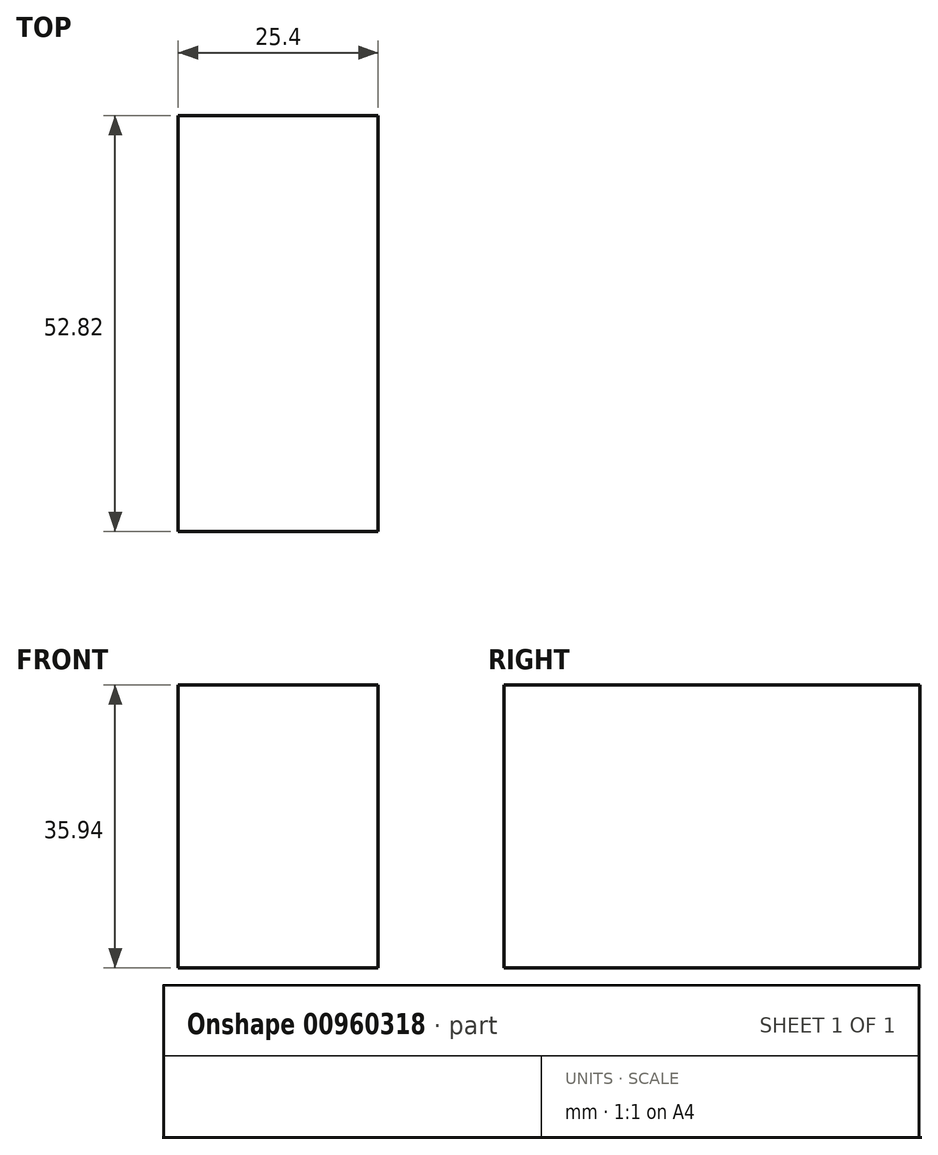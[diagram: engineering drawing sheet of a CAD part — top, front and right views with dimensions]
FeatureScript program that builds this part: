
annotation { "Feature Type Name" : "Feature", "Feature Type Description" : "" }
export const myFeature = defineFeature(function(context is Context, id is Id, definition is map)
    precondition{}
    {
        {
            var Q0;
            Q0=qCreatedBy(makeId("Right.planeOp"),FACE);
            var sketch = newSketch(context, id + "F0", { "sketchPlane" : qUnion([Q0])});
            skLineSegment(sketch, "E0.bottom", {"start": v(26.41, 17.97) * mm, "end": v(-26.41, 17.97) * mm});
            skLineSegment(sketch, "E0.top", {"start": v(26.41, -17.97) * mm, "end": v(-26.41, -17.97) * mm});
            skLineSegment(sketch, "E0.left", {"start": v(26.41, 17.97) * mm, "end": v(26.41, -17.97) * mm});
            skLineSegment(sketch, "E0.right", {"start": v(-26.41, 17.97) * mm, "end": v(-26.41, -17.97) * mm});
            skPoint(sketch, "E0.middle", {"position": v(0, 0) * mm});
            skSolve(sketch);
        }
        {
            var Q0;
            Q0=makeQuery(id+"F0.imprint","IMPRINT",FACE,{"disambiguationData":[TD([[makeQuery(id+"F0.imprint","IMPRINT",EDGE,{"derivedFrom":sQuery(id+"F0.wireOp",EDGE,"E0.bottom")}),1.0]])]});
            extrude(context, id + "F1", {"entities" : qUnion([Q0]), "depth" : 25.4 * mm, "offsetDistance" : 25.4 * mm});
        }
    });
